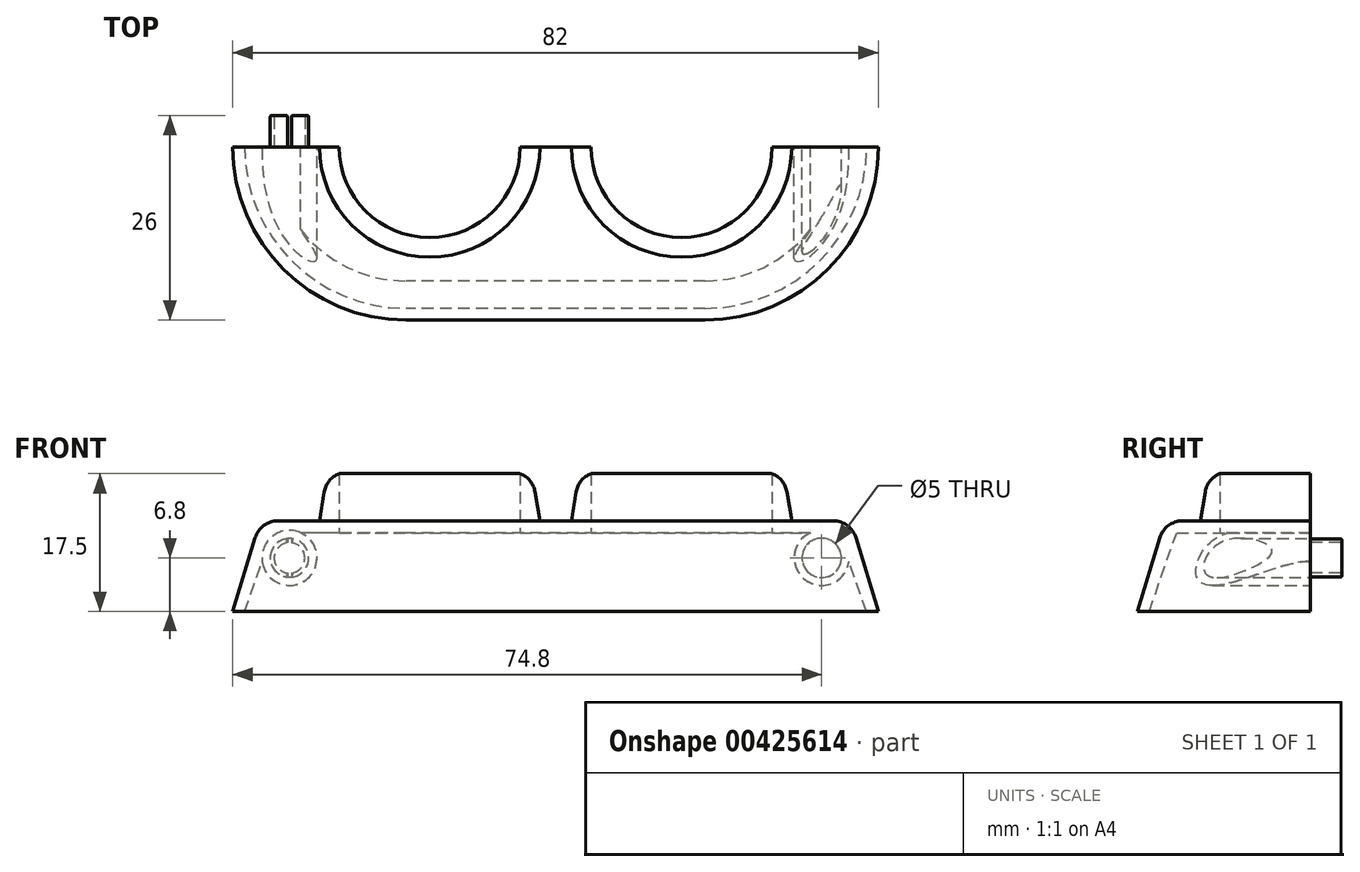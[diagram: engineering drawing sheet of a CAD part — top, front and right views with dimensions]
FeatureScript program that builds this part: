
annotation { "Feature Type Name" : "Feature", "Feature Type Description" : "" }
export const myFeature = defineFeature(function(context is Context, id is Id, definition is map)
    precondition{}
    {
        {
            var Q0;
            Q0=qCreatedBy(makeId("Top.planeOp"),FACE);
            var sketch = newSketch(context, id + "F0", { "sketchPlane" : qUnion([Q0])});
            skLineSegment(sketch, "E0", {"start": v(-4.5, 13.5) * mm, "end": v(4.5, 13.5) * mm});
            skArc(sketch, "E1", {"start": v(4.5, 13.5) * mm, "mid": v(16, 2) * mm, "end": v(27.5, 13.5) * mm});
            skArc(sketch, "E2", {"start": v(-27.5, 13.5) * mm, "mid": v(-16, 2) * mm, "end": v(-4.5, 13.5) * mm});
            skLineSegment(sketch, "E3", {"start": v(27.5, 13.5) * mm, "end": v(37.5, 13.5) * mm, "construction": true});
            skLineSegment(sketch, "E4", {"start": v(-27.5, 13.5) * mm, "end": v(-37.5, 13.5) * mm});
            skArc(sketch, "E5", {"start": v(-37.5, 13.5) * mm, "mid": v(-32.08, 0.42) * mm, "end": v(-19, -5) * mm});
            skArc(sketch, "E6", {"start": v(19, -5) * mm, "mid": v(32.08, 0.42) * mm, "end": v(37.5, 13.5) * mm});
            skLineSegment(sketch, "E7", {"start": v(-19, -5) * mm, "end": v(19, -5) * mm});
            skLineSegment(sketch, "E8", {"start": v(-37.5, 13.5) * mm, "end": v(37.5, 13.5) * mm, "construction": true});
            skLineSegment(sketch, "E9", {"start": v(27.5, 13.5) * mm, "end": v(37.5, 13.5) * mm});
            skSolve(sketch);
        }
        {
            var Q0;
            Q0 = qSketchRegion(id + "F0", true);
            extrude(context, id + "F1", {"entities" : qUnion([Q0]), "depth" : 1.5 * mm});
        }
        {
            var Q0;
            Q0=makeQuery(id+"F1.opExtrude","SWEPT_FACE",FACE,{"disambiguationData":[OSD([sQuery(id+"F0.wireOp",EDGE,"E9")])]});
            var sketch = newSketch(context, id + "F2", { "sketchPlane" : qUnion([Q0])});
            skLineSegment(sketch, "E10", {"start": v(-37.5, 1.5) * mm, "end": v(-41, -10) * mm});
            skLineSegment(sketch, "E11", {"start": v(-41, -10) * mm, "end": v(-36, -10) * mm, "construction": true});
            skLineSegment(sketch, "E12", {"start": v(-36, -10) * mm, "end": v(-36, 1.5) * mm, "construction": true});
            skLineSegment(sketch, "E13", {"start": v(-36, 1.5) * mm, "end": v(-37.5, 1.5) * mm});
            skLineSegment(sketch, "E14", {"start": v(-37.5, 0) * mm, "end": v(-37.5, -10) * mm, "construction": true});
            skLineSegment(sketch, "E15", {"start": v(-41, -10) * mm, "end": v(-39.5, -10) * mm});
            skLineSegment(sketch, "E16", {"start": v(-39.5, -10) * mm, "end": v(-36, 0) * mm});
            skCircle(sketch, "E17", {"center": v(-33.8, -3.2) * mm, "radius": 3.5 * mm});
            skCircle(sketch, "E18", {"center": v(-33.8, -3.2) * mm, "radius": 2.5 * mm});
            skLineSegment(sketch, "E19", {"start": v(-33.8, -3.2) * mm, "end": v(41.2, -3.2) * mm, "construction": true});
            skCircle(sketch, "E20", {"center": v(33.8, -3.2) * mm, "radius": 2.45 * mm});
            skCircle(sketch, "E21", {"center": v(33.8, -3.2) * mm, "radius": 3.5 * mm});
            skLineSegment(sketch, "E22.bottom", {"start": v(35.22, 0) * mm, "end": v(36.42, 0) * mm});
            skLineSegment(sketch, "E22.top", {"start": v(35.22, -0.88) * mm, "end": v(36.42, -0.88) * mm});
            skLineSegment(sketch, "E22.left", {"start": v(35.22, 0) * mm, "end": v(35.22, -0.88) * mm});
            skLineSegment(sketch, "E22.right", {"start": v(36.42, 0) * mm, "end": v(36.42, -0.88) * mm});
            skCircle(sketch, "E23", {"center": v(33.8, -3.2) * mm, "radius": 1.95 * mm});
            skLineSegment(sketch, "E24", {"start": v(33.8, 0.3) * mm, "end": v(33.8, -6.7) * mm, "construction": true});
            skLineSegment(sketch, "E25", {"start": v(33.55, -0.76) * mm, "end": v(33.55, -1.27) * mm});
            skLineSegment(sketch, "E26", {"start": v(34.05, -0.76) * mm, "end": v(34.05, -1.27) * mm});
            skLineSegment(sketch, "E27", {"start": v(33.55, -5.13) * mm, "end": v(33.55, -5.64) * mm});
            skLineSegment(sketch, "E28", {"start": v(34.05, -5.13) * mm, "end": v(34.05, -5.64) * mm});
            skSolve(sketch);
        }
        {
            var Q0;
            Q0=makeQuery(id+"F2.imprint","IMPRINT",FACE,{"disambiguationData":[TD([[makeQuery(id+"F2.imprint","IMPRINT",EDGE,{"derivedFrom":sQuery(id+"F2.wireOp",EDGE,"E10")}),1.0]])]});
            var Q1;
            {var subQ0=sQuery(id+"F2.wireOp",EDGE,"E17");var subQ1=sQuery(id+"F2.wireOp",EDGE,"E16");var subQ2=makeQuery(id+"F2.imprint","INTERSECT",VERTEX,{"disambiguationData":[OD(0.0)],"derivedFrom":[subQ1,subQ0]});Q1=makeQuery(id+"F2.imprint","IMPRINT",FACE,{"disambiguationData":[TD([[makeQuery(id+"F2.imprint","IMPRINT",EDGE,{"disambiguationData":[TD([[subQ2,-1.0]])],"derivedFrom":subQ1}),1.0]])]});}
            var Q2;
            {var subQ0=sQuery(id+"F2.wireOp",EDGE,"E18");var subQ1=sQuery(id+"F2.wireOp",EDGE,"E16");var subQ2=makeQuery(id+"F2.imprint","INTERSECT",VERTEX,{"disambiguationData":[OD(0.0)],"derivedFrom":[subQ1,subQ0]});Q2=makeQuery(id+"F2.imprint","IMPRINT",FACE,{"disambiguationData":[TD([[makeQuery(id+"F2.imprint","IMPRINT",EDGE,{"disambiguationData":[TD([[subQ2,-1.0]])],"derivedFrom":subQ1}),1.0]])]});}
            var Q3;
            Q3=makeQuery(id+"F1.opExtrude","CAP_EDGE",EDGE,{"disambiguationData":[OSD([sQuery(id+"F0.wireOp",EDGE,"E6")])],"isStart":true});
            var Q4;
            Q4=makeQuery(id+"F1.opExtrude","CAP_EDGE",EDGE,{"disambiguationData":[OSD([sQuery(id+"F0.wireOp",EDGE,"E7")])],"isStart":true});
            var Q5;
            Q5=makeQuery(id+"F1.opExtrude","CAP_EDGE",EDGE,{"disambiguationData":[OSD([sQuery(id+"F0.wireOp",EDGE,"E5")])],"isStart":true});
            sweep(context, id + "F3", {"operationType" : NewBodyOperationType.ADD, "profiles" : qUnion([Q0, Q1, Q2]), "path" : qUnion([Q3, Q4, Q5])});
        }
        {
            var Q0;
            Q0=makeQuery(id+"F2.imprint","IMPRINT",FACE,{"disambiguationData":[TD([[makeQuery(id+"F2.imprint","IMPRINT",EDGE,{"derivedFrom":sQuery(id+"F2.wireOp",EDGE,"E18")}),-1.0]])]});
            var Q1;
            {var subQ0=sQuery(id+"F2.wireOp",EDGE,"E16");var subQ1=makeQuery(id+"F1.opExtrude","CAP_EDGE",EDGE,{"disambiguationData":[OSD([sQuery(id+"F0.wireOp",EDGE,"E9")])],"isStart":true});var subQ2=makeQuery(id+"F2.imprint","INTERSECT",VERTEX,{"derivedFrom":[subQ1,subQ0]});Q1=makeQuery(id+"F2.imprint","IMPRINT",FACE,{"disambiguationData":[TD([[makeQuery(id+"F2.imprint","IMPRINT",EDGE,{"disambiguationData":[TD([[subQ2,1.0]])],"derivedFrom":subQ0}),-1.0]])]});}
            var Q2;
            Q2=makeQuery(id+"F3.opSweep","SWEPT_FACE",FACE,{"disambiguationData":[OSD([sQuery(id+"F0.wireOp",EDGE,"E6"),sQuery(id+"F2.wireOp",EDGE,"E16")])]});
            extrude(context, id + "F4", {"entities" : qUnion([Q0, Q1]), "operationType" : NewBodyOperationType.ADD, "endBound" : BoundingType.UP_TO_SURFACE, "oppositeDirection" : true, "endBoundEntityFace" : qUnion([Q2]), "depth" : 25 * mm});
        }
        {
            var Q0;
            Q0=makeQuery(id+"F2.imprint","IMPRINT",FACE,{"disambiguationData":[TD([[makeQuery(id+"F2.imprint","IMPRINT",EDGE,{"derivedFrom":sQuery(id+"F2.wireOp",EDGE,"E20")}),-1.0]])]});
            var Q1;
            Q1=makeQuery(id+"F2.imprint","IMPRINT",FACE,{"disambiguationData":[TD([[makeQuery(id+"F2.imprint","IMPRINT",EDGE,{"derivedFrom":sQuery(id+"F2.wireOp",EDGE,"E20")}),1.0]])]});
            var Q2;
            {var subQ0=sQuery(id+"F2.wireOp",EDGE,"E22.bottom");Q2=makeQuery(id+"F2.imprint","IMPRINT",FACE,{"disambiguationData":[TD([[makeQuery(id+"F2.imprint","IMPRINT",EDGE,{"derivedFrom":subQ0}),-1.0]])]});}
            var Q3;
            {var subQ2=sQuery(id+"F2.wireOp",EDGE,"E22.top");Q3=makeQuery(id+"F2.imprint","IMPRINT",FACE,{"disambiguationData":[TD([[makeQuery(id+"F2.imprint","IMPRINT",EDGE,{"derivedFrom":subQ2}),1.0]])]});}
            var Q4;
            Q4=makeQuery(id+"F2.imprint","IMPRINT",FACE,{"disambiguationData":[TD([[makeQuery(id+"F2.imprint","IMPRINT",EDGE,{"derivedFrom":sQuery(id+"F2.wireOp",EDGE,"E23")}),1.0]])]});
            var Q5;
            {var subQ1=sQuery(id+"F2.wireOp",EDGE,"6IaGaOor-0Jtq-2Uqc-Dhca-cXkXNbNAKBQb.bottom");Q5=makeQuery(id+"F2.imprint","IMPRINT",FACE,{"disambiguationData":[TD([[makeQuery(id+"F2.imprint","IMPRINT",EDGE,{"derivedFrom":subQ1}),-1.0]])]});}
            var Q6;
            {var subQ1=sQuery(id+"F2.wireOp",EDGE,"ITs5NmBU-5ak0-nM55-Ze9f-cnBISc9jjtty.bottom");Q6=makeQuery(id+"F2.imprint","IMPRINT",FACE,{"disambiguationData":[TD([[makeQuery(id+"F2.imprint","IMPRINT",EDGE,{"derivedFrom":subQ1}),-1.0]])]});}
            var Q7;
            Q7=makeQuery(id+"F3.opSweep","SWEPT_FACE",FACE,{"disambiguationData":[OSD([sQuery(id+"F0.wireOp",EDGE,"E5"),sQuery(id+"F2.wireOp",EDGE,"E16")])]});
            extrude(context, id + "F5", {"entities" : qUnion([Q0, Q1, Q2, Q3, Q4, Q5, Q6]), "operationType" : NewBodyOperationType.ADD, "endBound" : BoundingType.UP_TO_SURFACE, "oppositeDirection" : true, "endBoundEntityFace" : qUnion([Q7]), "depth" : 25 * mm});
        }
        {
            var Q0;
            {var subQ0=sQuery(id+"F2.wireOp",EDGE,"E26");Q0=makeQuery(id+"F2.imprint","IMPRINT",FACE,{"disambiguationData":[TD([[makeQuery(id+"F2.imprint","IMPRINT",EDGE,{"derivedFrom":subQ0}),1.0]])]});}
            var Q1;
            {var subQ0=sQuery(id+"F2.wireOp",EDGE,"E25");Q1=makeQuery(id+"F2.imprint","IMPRINT",FACE,{"disambiguationData":[TD([[makeQuery(id+"F2.imprint","IMPRINT",EDGE,{"derivedFrom":subQ0}),-1.0]])]});}
            extrude(context, id + "F6", {"entities" : qUnion([Q0, Q1]), "operationType" : NewBodyOperationType.ADD, "depth" : 4 * mm});
        }
        {
            var Q0;
            Q0=makeQuery(id+"F6.opExtrude","CAP_FACE",FACE,{"disambiguationData":[OSD([sQuery(id+"F2.wireOp",EDGE,"E20"),sQuery(id+"F2.wireOp",EDGE,"E23"),sQuery(id+"F2.wireOp",EDGE,"6IaGaOor-0Jtq-2Uqc-Dhca-cXkXNbNAKBQb.top"),sQuery(id+"F2.wireOp",EDGE,"ITs5NmBU-5ak0-nM55-Ze9f-cnBISc9jjtty.top")])],"isStart":false});
            var Q1;
            Q1=makeQuery(id+"F6.opExtrude","CAP_FACE",FACE,{"disambiguationData":[OSD([sQuery(id+"F2.wireOp",EDGE,"E20"),sQuery(id+"F2.wireOp",EDGE,"E23"),sQuery(id+"F2.wireOp",EDGE,"6IaGaOor-0Jtq-2Uqc-Dhca-cXkXNbNAKBQb.bottom"),sQuery(id+"F2.wireOp",EDGE,"ITs5NmBU-5ak0-nM55-Ze9f-cnBISc9jjtty.bottom")])],"isStart":false});
            fillet(context, id + "F7", {"entities" : qUnion([Q0, Q1]), "radius" : 0.2 * mm, "tangentPropagation" : true, "allowEdgeOverflow" : false});
        }
        {
            var Q0;
            Q0=makeQuery(id+"F1.opExtrude","CAP_FACE",FACE,{"disambiguationData":[OSD([sQuery(id+"F0.wireOp",EDGE,"E0"),sQuery(id+"F0.wireOp",EDGE,"E1"),sQuery(id+"F0.wireOp",EDGE,"E2"),sQuery(id+"F0.wireOp",EDGE,"E4"),sQuery(id+"F0.wireOp",EDGE,"E5"),sQuery(id+"F0.wireOp",EDGE,"E6"),sQuery(id+"F0.wireOp",EDGE,"E7"),sQuery(id+"F0.wireOp",EDGE,"E9")])],"isStart":false});
            var sketch = newSketch(context, id + "F8", { "sketchPlane" : qUnion([Q0])});
            skArc(sketch, "E29.0", {"start": v(-30, 13.5) * mm, "mid": v(-16, -0.5) * mm, "end": v(-2, 13.5) * mm});
            skArc(sketch, "E30.0", {"start": v(-27.5, 13.5) * mm, "mid": v(-16, 2) * mm, "end": v(-4.5, 13.5) * mm});
            skArc(sketch, "E31.0", {"start": v(4.5, 13.5) * mm, "mid": v(16, 2) * mm, "end": v(27.5, 13.5) * mm});
            skArc(sketch, "E32.0", {"start": v(2, 13.5) * mm, "mid": v(16, -0.5) * mm, "end": v(30, 13.5) * mm});
            skLineSegment(sketch, "E33", {"start": v(-30, 13.5) * mm, "end": v(-27.5, 13.5) * mm});
            skLineSegment(sketch, "E34", {"start": v(-4.5, 13.5) * mm, "end": v(-2, 13.5) * mm});
            skLineSegment(sketch, "E35", {"start": v(2, 13.5) * mm, "end": v(4.5, 13.5) * mm});
            skLineSegment(sketch, "E36", {"start": v(27.5, 13.5) * mm, "end": v(30, 13.5) * mm});
            skSolve(sketch);
        }
        {
            var Q0;
            Q0 = qSketchRegion(id + "F8", true);
            extrude(context, id + "F9", {"entities" : qUnion([Q0]), "operationType" : NewBodyOperationType.ADD, "depth" : 6 * mm});
        }
        {
            var Q0;
            Q0=makeQuery(id+"F9.opExtrude","CAP_EDGE",EDGE,{"disambiguationData":[OSD([sQuery(id+"F8.wireOp",EDGE,"E29.0")])],"isStart":false});
            var Q1;
            Q1=makeQuery(id+"F9.opExtrude","CAP_EDGE",EDGE,{"disambiguationData":[OSD([sQuery(id+"F8.wireOp",EDGE,"E32.0")])],"isStart":false});
            chamfer(context, id + "F10", {"entities" : qUnion([Q0, Q1]), "chamferType" : ChamferType.TWO_OFFSETS, "width1" : 1 * mm, "oppositeDirection" : false, "width2" : 6 * mm, "tangentPropagation" : true});
        }
        {
            var Q0;
            {var subQ0=sQuery(id+"F0.wireOp",EDGE,"E6");Q0=makeQuery(id+"F3.boolean.opBoolean","MERGE",EDGE,{"derivedFrom":[makeQuery(id+"F1.opExtrude","CAP_EDGE",EDGE,{"disambiguationData":[OSD([subQ0])],"isStart":false}),makeQuery(id+"F3.opSweep","SWEPT_EDGE",EDGE,{"disambiguationData":[OSD([subQ0,sQuery(id+"F0.wireOp",EDGE,"E9"),sQuery(id+"F2.wireOp",EDGE,"E10"),sQuery(id+"F2.wireOp",EDGE,"E13")])]})]});}
            var Q1;
            {var subQ0=sQuery(id+"F0.wireOp",EDGE,"E7");Q1=makeQuery(id+"F3.boolean.opBoolean","MERGE",EDGE,{"derivedFrom":[makeQuery(id+"F1.opExtrude","CAP_EDGE",EDGE,{"disambiguationData":[OSD([subQ0])],"isStart":false}),makeQuery(id+"F3.opSweep","SWEPT_EDGE",EDGE,{"disambiguationData":[OSD([sQuery(id+"F0.wireOp",EDGE,"E6"),subQ0,sQuery(id+"F0.wireOp",EDGE,"E9"),sQuery(id+"F2.wireOp",EDGE,"E10"),sQuery(id+"F2.wireOp",EDGE,"E13")])]})]});}
            var Q2;
            {var subQ0=sQuery(id+"F0.wireOp",EDGE,"E5");Q2=makeQuery(id+"F3.boolean.opBoolean","MERGE",EDGE,{"derivedFrom":[makeQuery(id+"F1.opExtrude","CAP_EDGE",EDGE,{"disambiguationData":[OSD([subQ0])],"isStart":false}),makeQuery(id+"F3.opSweep","SWEPT_EDGE",EDGE,{"disambiguationData":[OSD([subQ0,sQuery(id+"F0.wireOp",EDGE,"E6"),sQuery(id+"F0.wireOp",EDGE,"E9"),sQuery(id+"F2.wireOp",EDGE,"E10"),sQuery(id+"F2.wireOp",EDGE,"E13")])]})]});}
            var Q3;
            {var subQ0=sQuery(id+"F8.wireOp",EDGE,"E29.0");Q3=makeQuery(id+"F10.opChamfer","BLEND_EDGE",EDGE,{"blendedFrom":[makeQuery(id+"F9.opExtrude","CAP_EDGE",EDGE,{"disambiguationData":[OSD([subQ0])],"isStart":false}),makeQuery(id+"F9.opExtrude","CAP_FACE",FACE,{"disambiguationData":[OSD([subQ0,sQuery(id+"F8.wireOp",EDGE,"E30.0"),sQuery(id+"F8.wireOp",EDGE,"E33"),sQuery(id+"F8.wireOp",EDGE,"E34")])],"isStart":false})],"blendedInto":[makeQuery(id+"F9.opExtrude","CAP_FACE",FACE,{"disambiguationData":[OSD([subQ0,sQuery(id+"F8.wireOp",EDGE,"E30.0"),sQuery(id+"F8.wireOp",EDGE,"E33"),sQuery(id+"F8.wireOp",EDGE,"E34")])],"isStart":false})]});}
            var Q4;
            {var subQ0=sQuery(id+"F8.wireOp",EDGE,"E32.0");Q4=makeQuery(id+"F10.opChamfer","BLEND_EDGE",EDGE,{"blendedFrom":[makeQuery(id+"F9.opExtrude","CAP_EDGE",EDGE,{"disambiguationData":[OSD([subQ0])],"isStart":false}),makeQuery(id+"F9.opExtrude","CAP_FACE",FACE,{"disambiguationData":[OSD([sQuery(id+"F8.wireOp",EDGE,"E31.0"),subQ0,sQuery(id+"F8.wireOp",EDGE,"E35"),sQuery(id+"F8.wireOp",EDGE,"E36")])],"isStart":false})],"blendedInto":[makeQuery(id+"F9.opExtrude","CAP_FACE",FACE,{"disambiguationData":[OSD([sQuery(id+"F8.wireOp",EDGE,"E31.0"),subQ0,sQuery(id+"F8.wireOp",EDGE,"E35"),sQuery(id+"F8.wireOp",EDGE,"E36")])],"isStart":false})]});}
            fillet(context, id + "F11", {"entities" : qUnion([Q0, Q1, Q2, Q3, Q4]), "radius" : 3 * mm, "tangentPropagation" : true, "allowEdgeOverflow" : false});
        }
        {
            var Q0;
            {var subQ7=sQuery(id+"F2.wireOp",EDGE,"E22.top");Q0=makeQuery(id+"F2.imprint","IMPRINT",FACE,{"disambiguationData":[TD([[makeQuery(id+"F2.imprint","IMPRINT",EDGE,{"derivedFrom":subQ7}),-1.0]])]});}
            var Q1;
            {var subQ2=sQuery(id+"F2.wireOp",EDGE,"E22.top");Q1=makeQuery(id+"F2.imprint","IMPRINT",FACE,{"disambiguationData":[TD([[makeQuery(id+"F2.imprint","IMPRINT",EDGE,{"derivedFrom":subQ2}),1.0]])]});}
            var Q2;
            Q2=sQuery(id+"F2.wireOp",EDGE,"E21");
            extrude(context, id + "F12", {"entities" : qUnion([Q0, Q1]), "operationType" : NewBodyOperationType.REMOVE, "surfaceEntities" : qUnion([Q2]), "oppositeDirection" : true, "depth" : 0.1 * mm});
        }
    });
